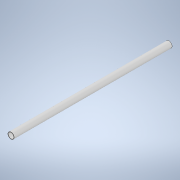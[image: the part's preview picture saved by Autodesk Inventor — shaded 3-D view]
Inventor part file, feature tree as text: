
AUTODESK INVENTOR PART (.ipt)
format: ipt  version: 2022 (Build 260153000, 153)  size: 100,352 bytes
history: native  units: in
note: dims shown in document units (in); Inventor stores cm internally (conversion verified against a paired STEP export)
features: extrude x1
ambient origin geometry x8: Origin, YZ Plane, XZ Plane, XY Plane, X Axis, Y Axis, Z Axis, Center Point
bodies: Solid1 (feature_tree)
feature tree (1):
  extrude  "Extrude-Thin1"  [1 undecoded]
note: 1 required parameter value undecoded (feature->parameter linkage not recoverable at this tier; creation-order binding heuristic only, values carry confidence <= 0.55)
